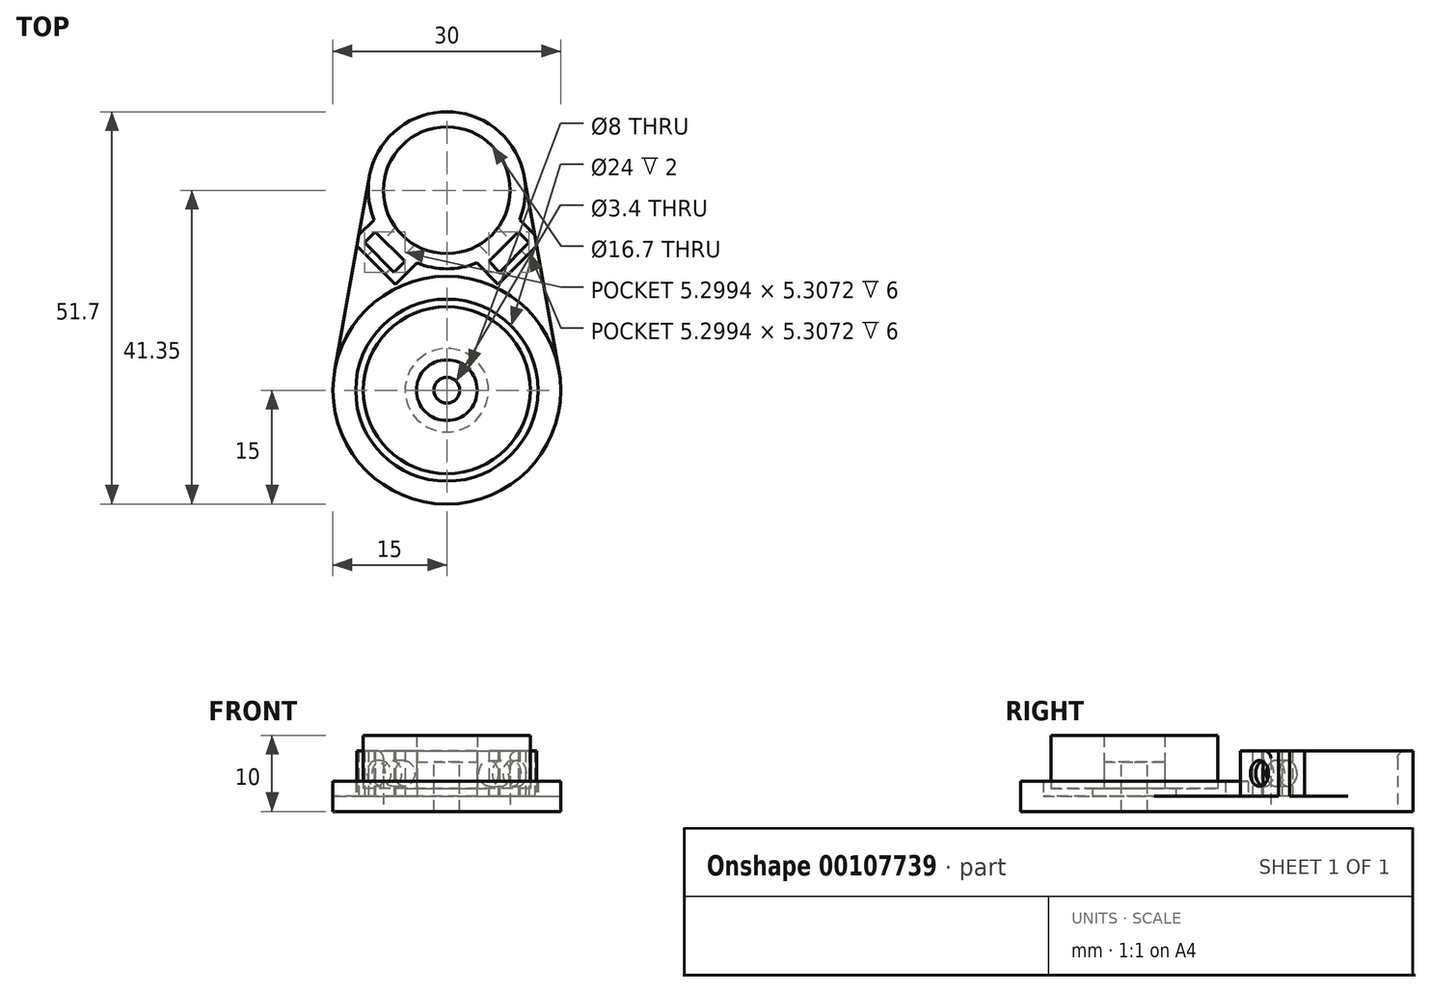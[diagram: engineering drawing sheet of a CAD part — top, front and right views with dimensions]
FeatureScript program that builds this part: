
annotation { "Feature Type Name" : "Feature", "Feature Type Description" : "" }
export const myFeature = defineFeature(function(context is Context, id is Id, definition is map)
    precondition{}
    {
        {
            assignVariable(context, id + "F0", {"name" : "BearingHeight", "anyValue" : 7});
        }
        {
            var Q0;
            Q0=qCreatedBy(makeId("Front.planeOp"),FACE);
            var sketch = newSketch(context, id + "F1", { "sketchPlane" : qUnion([Q0])});
            skLineSegment(sketch, "E0", {"start": v(0, 0) * mm, "end": v(0, 6.5) * mm});
            skLineSegment(sketch, "E1", {"start": v(0, 6.5) * mm, "end": v(4, 6.5) * mm});
            skLineSegment(sketch, "E2", {"start": v(4, 6.5) * mm, "end": v(4, 3) * mm});
            skLineSegment(sketch, "E3", {"start": v(4, 3) * mm, "end": v(5.5, 3) * mm});
            skLineSegment(sketch, "E4", {"start": v(5.5, 3) * mm, "end": v(5.5, 2) * mm});
            skLineSegment(sketch, "E5", {"start": v(5.5, 2) * mm, "end": v(11, 2) * mm});
            skLineSegment(sketch, "E6", {"start": v(11, 2) * mm, "end": v(12, 2) * mm});
            skLineSegment(sketch, "E7", {"start": v(12, 2) * mm, "end": v(12, 4) * mm});
            skLineSegment(sketch, "E8", {"start": v(12, 4) * mm, "end": v(15, 4) * mm});
            skLineSegment(sketch, "E9", {"start": v(15, 4) * mm, "end": v(15, 0) * mm});
            skLineSegment(sketch, "E10", {"start": v(15, 0) * mm, "end": v(0, 0) * mm});
            skSolve(sketch);
        }
        {
            var Q0;
            Q0=qSketchRegion(id+"F1",true);
            var Q1;
            Q1=sQuery(id+"F1.wireOp",EDGE,"E0");
            revolve(context, id + "F2", {"entities" : qUnion([Q0]), "axis" : qUnion([Q1]), "revolveType" : RevolveType.FULL});
        }
        {
            var Q0;
            Q0=makeQuery(id+"F2.opRevolve","SWEPT_FACE",FACE,{"disambiguationData":[OSD([sQuery(id+"F1.wireOp",EDGE,"E1")])]});
            var sketch = newSketch(context, id + "F3", { "sketchPlane" : qUnion([Q0])});
            skCircle(sketch, "E11", {"center": v(0, 0) * mm, "radius": 1.7 * mm});
            skSolve(sketch);
        }
        {
            var Q0;
            Q0=makeQuery(id+"F3.imprint","IMPRINT",FACE,{"disambiguationData":[TD([[makeQuery(id+"F3.imprint","IMPRINT",EDGE,{"derivedFrom":sQuery(id+"F3.wireOp",EDGE,"E11")}),1.0]])]});
            extrude(context, id + "F4", {"entities" : qUnion([Q0]), "operationType" : NewBodyOperationType.REMOVE, "endBound" : BoundingType.UP_TO_NEXT, "oppositeDirection" : true, "depth" : 25 * mm});
        }
        {
            var Q0;
            Q0=makeQuery(id+"F2.opRevolve","SWEPT_FACE",FACE,{"disambiguationData":[OSD([sQuery(id+"F1.wireOp",EDGE,"E10")])]});
            var sketch = newSketch(context, id + "F5", { "sketchPlane" : qUnion([Q0])});
            skCircle(sketch, "E12.0", {"center": v(0, 0) * mm, "radius": 15 * mm});
            skLineSegment(sketch, "E13", {"start": v(0, -26.35) * mm, "end": v(0, 0) * mm, "construction": true});
            skCircle(sketch, "E14", {"center": v(0, -26.35) * mm, "radius": 10.35 * mm});
            skLineSegment(sketch, "E15", {"start": v(-14.76, -2.65) * mm, "end": v(-10.19, -28.18) * mm});
            skLineSegment(sketch, "E16", {"start": v(14.76, -2.65) * mm, "end": v(10.19, -28.18) * mm});
            skCircle(sketch, "E17", {"center": v(0, -26.35) * mm, "radius": 8.35 * mm});
            skLineSegment(sketch, "E18", {"start": v(-3.94, -16.78) * mm, "end": v(-6.77, -13.95) * mm});
            skLineSegment(sketch, "E19", {"start": v(-6.77, -13.95) * mm, "end": v(-12.42, -19.62) * mm});
            skLineSegment(sketch, "E20", {"start": v(-12.42, -19.62) * mm, "end": v(-9.58, -22.44) * mm});
            skLineSegment(sketch, "E21", {"start": v(0, -26.35) * mm, "end": v(-9.6, -16.79) * mm, "construction": true});
            skLineSegment(sketch, "E22.bottom", {"start": v(-9.41, -20.85) * mm, "end": v(-5.53, -16.96) * mm});
            skLineSegment(sketch, "E22.top", {"start": v(-10.83, -19.44) * mm, "end": v(-6.94, -15.55) * mm});
            skLineSegment(sketch, "E22.left", {"start": v(-9.41, -20.85) * mm, "end": v(-10.83, -19.44) * mm});
            skLineSegment(sketch, "E22.right", {"start": v(-5.53, -16.96) * mm, "end": v(-6.94, -15.55) * mm});
            skPoint(sketch, "E22.middle", {"position": v(-8.18, -18.2) * mm});
            skLineSegment(sketch, "E23.MirrorCS", {"start": v(5.53, -16.96) * mm, "end": v(6.94, -15.55) * mm});
            skLineSegment(sketch, "E24.MirrorCS", {"start": v(3.94, -16.78) * mm, "end": v(6.77, -13.95) * mm});
            skPoint(sketch, "E25.MirrorP", {"position": v(8.18, -18.2) * mm});
            skLineSegment(sketch, "E26.MirrorCS", {"start": v(12.42, -19.62) * mm, "end": v(9.58, -22.44) * mm});
            skLineSegment(sketch, "E27.MirrorCS", {"start": v(9.41, -20.85) * mm, "end": v(10.83, -19.44) * mm});
            skLineSegment(sketch, "E28.MirrorCS", {"start": v(10.83, -19.44) * mm, "end": v(6.94, -15.55) * mm});
            skLineSegment(sketch, "E29.MirrorCS", {"start": v(6.77, -13.95) * mm, "end": v(12.42, -19.62) * mm});
            skLineSegment(sketch, "E30.MirrorCS", {"start": v(9.41, -20.85) * mm, "end": v(5.53, -16.96) * mm});
            skSolve(sketch);
        }
        {
            var Q0;
            {var subQ0=sQuery(id+"F5.wireOp",EDGE,"E16");Q0=makeQuery(id+"F5.imprint","IMPRINT",FACE,{"disambiguationData":[TD([[makeQuery(id+"F5.imprint","IMPRINT",EDGE,{"derivedFrom":subQ0}),-1.0]])]});}
            var Q1;
            Q1=makeQuery(id+"F5.imprint","IMPRINT",FACE,{"disambiguationData":[TD([[makeQuery(id+"F5.imprint","IMPRINT",EDGE,{"derivedFrom":sQuery(id+"F5.wireOp",EDGE,"E17")}),-1.0]])]});
            var Q2;
            {var subQ0=sQuery(id+"F5.wireOp",EDGE,"E18");Q2=makeQuery(id+"F5.imprint","IMPRINT",FACE,{"disambiguationData":[TD([[makeQuery(id+"F5.imprint","IMPRINT",EDGE,{"derivedFrom":subQ0}),1.0]])]});}
            var Q3;
            {var subQ1=sQuery(id+"F5.wireOp",EDGE,"E22.bottom");Q3=makeQuery(id+"F5.imprint","IMPRINT",FACE,{"disambiguationData":[TD([[makeQuery(id+"F5.imprint","IMPRINT",EDGE,{"derivedFrom":subQ1}),1.0]])]});}
            var Q4;
            {var subQ0=sQuery(id+"F5.wireOp",EDGE,"E15");var subQ1=sQuery(id+"F5.wireOp",EDGE,"E14");var subQ2=makeQuery(id+"F5.imprint","INTERSECT",VERTEX,{"derivedFrom":[subQ1,subQ0]});Q4=makeQuery(id+"F5.imprint","IMPRINT",FACE,{"disambiguationData":[TD([[makeQuery(id+"F5.imprint","IMPRINT",EDGE,{"disambiguationData":[TD([[subQ2,1.0]])],"derivedFrom":subQ1}),-1.0]])]});}
            var Q5;
            Q5=makeQuery(id+"F5.imprint","IMPRINT",FACE,{"disambiguationData":[TD([[makeQuery(id+"F5.imprint","IMPRINT",EDGE,{"derivedFrom":makeQuery(id+"F4.boolean.opBoolean","COPY",EDGE,{"derivedFrom":makeQuery(id+"F4.opExtrude","TWEAK_EDGE",EDGE,{"derivedFrom":[makeQuery(id+"F2.opRevolve","SWEPT_FACE",FACE,{"disambiguationData":[OSD([sQuery(id+"F1.wireOp",EDGE,"E10")])]}),makeQuery(id+"F3.imprint","IMPRINT",EDGE,{"derivedFrom":sQuery(id+"F3.wireOp",EDGE,"E11")})]})})}),-1.0]])]});
            var Q6;
            Q6=makeQuery(id+"F2.opRevolve","SWEPT_FACE",FACE,{"disambiguationData":[OSD([sQuery(id+"F1.wireOp",EDGE,"E10")])]});
            var Q7;
            Q7=makeQuery(id+"F5.imprint","IMPRINT",FACE,{"disambiguationData":[TD([[makeQuery(id+"F5.imprint","IMPRINT",EDGE,{"derivedFrom":sQuery(id+"F5.wireOp",EDGE,"E23.MirrorCS")}),1.0]])]});
            var Q8;
            Q8=makeQuery(id+"F5.imprint","IMPRINT",FACE,{"disambiguationData":[TD([[makeQuery(id+"F5.imprint","IMPRINT",EDGE,{"derivedFrom":sQuery(id+"F5.wireOp",EDGE,"E23.MirrorCS")}),-1.0]])]});
            var Q9;
            {var subQ10=sQuery(id+"F5.wireOp",EDGE,"E18");Q9=makeQuery(id+"F5.imprint","IMPRINT",FACE,{"disambiguationData":[TD([[makeQuery(id+"F5.imprint","IMPRINT",EDGE,{"derivedFrom":subQ10}),-1.0]])]});}
            var Q10;
            Q10=makeQuery(id+"F2.opRevolve","SWEPT_FACE",FACE,{"disambiguationData":[OSD([sQuery(id+"F1.wireOp",EDGE,"E5"),sQuery(id+"F1.wireOp",EDGE,"E6")])]});
            extrude(context, id + "F6", {"entities" : qUnion([Q0, Q1, Q2, Q3, Q4, Q5, Q6, Q7, Q8, Q9]), "operationType" : NewBodyOperationType.ADD, "endBound" : BoundingType.UP_TO_SURFACE, "oppositeDirection" : true, "endBoundEntityFace" : qUnion([Q10]), "depth" : 25 * mm});
        }
        {
            var Q0;
            Q0=makeQuery(id+"F5.imprint","IMPRINT",FACE,{"disambiguationData":[TD([[makeQuery(id+"F5.imprint","IMPRINT",EDGE,{"derivedFrom":sQuery(id+"F5.wireOp",EDGE,"E17")}),-1.0]])]});
            var Q1;
            {var subQ0=sQuery(id+"F5.wireOp",EDGE,"E18");Q1=makeQuery(id+"F5.imprint","IMPRINT",FACE,{"disambiguationData":[TD([[makeQuery(id+"F5.imprint","IMPRINT",EDGE,{"derivedFrom":subQ0}),1.0]])]});}
            var Q2;
            Q2=makeQuery(id+"F5.imprint","IMPRINT",FACE,{"disambiguationData":[TD([[makeQuery(id+"F5.imprint","IMPRINT",EDGE,{"derivedFrom":sQuery(id+"F5.wireOp",EDGE,"E23.MirrorCS")}),1.0]])]});
            extrude(context, id + "F7", {"entities" : qUnion([Q0, Q1, Q2]), "operationType" : NewBodyOperationType.ADD, "oppositeDirection" : true, "depth" : 8 * mm});
        }
        {
            var Q0;
            Q0=makeQuery(id+"F7.opExtrude","SWEPT_FACE",FACE,{"disambiguationData":[OSD([sQuery(id+"F5.wireOp",EDGE,"E19")])]});
            var sketch = newSketch(context, id + "F8", { "sketchPlane" : qUnion([Q0])});
            skLineSegment(sketch, "E31", {"start": v(-14.66, 5) * mm, "end": v(-21.83, 5) * mm, "construction": true});
            skPoint(sketch, "E32", {"position": v(-18.24, 5) * mm});
            skCircle(sketch, "E33", {"center": v(-18.24, 5) * mm, "radius": 1.7 * mm});
            skSolve(sketch);
        }
        {
            var Q0;
            Q0=makeQuery(id+"F8.imprint","IMPRINT",FACE,{"disambiguationData":[TD([[makeQuery(id+"F8.imprint","IMPRINT",EDGE,{"derivedFrom":sQuery(id+"F8.wireOp",EDGE,"E33")}),1.0]])]});
            var Q1;
            {var subQ0=sQuery(id+"F5.wireOp",EDGE,"E17");Q1=makeQuery(id+"F7.boolean.opBoolean","MERGE",FACE,{"derivedFrom":[makeQuery(id+"F6.opExtrude","SWEPT_FACE",FACE,{"disambiguationData":[OSD([subQ0])]}),makeQuery(id+"F7.opExtrude","SWEPT_FACE",FACE,{"disambiguationData":[OSD([subQ0])]})]});}
            extrude(context, id + "F9", {"entities" : qUnion([Q0]), "operationType" : NewBodyOperationType.REMOVE, "endBound" : BoundingType.UP_TO_SURFACE, "oppositeDirection" : true, "endBoundEntityFace" : qUnion([Q1]), "depth" : 25 * mm});
        }
        {
            var Q0;
            Q0=makeQuery(id+"F7.opExtrude","SWEPT_FACE",FACE,{"disambiguationData":[OSD([sQuery(id+"F5.wireOp",EDGE,"E29.MirrorCS")])]});
            var sketch = newSketch(context, id + "F10", { "sketchPlane" : qUnion([Q0])});
            skLineSegment(sketch, "E34", {"start": v(18.24, 2) * mm, "end": v(18.24, 8) * mm, "construction": true});
            skPoint(sketch, "E35", {"position": v(18.24, 5) * mm});
            skCircle(sketch, "E36", {"center": v(18.24, 5) * mm, "radius": 1.7 * mm});
            skSolve(sketch);
        }
        {
            var Q0;
            Q0=makeQuery(id+"F10.imprint","IMPRINT",FACE,{"disambiguationData":[TD([[makeQuery(id+"F10.imprint","IMPRINT",EDGE,{"derivedFrom":sQuery(id+"F10.wireOp",EDGE,"E36")}),1.0]])]});
            var Q1;
            {var subQ0=sQuery(id+"F5.wireOp",EDGE,"E17");Q1=makeQuery(id+"F7.boolean.opBoolean","MERGE",FACE,{"derivedFrom":[makeQuery(id+"F6.opExtrude","SWEPT_FACE",FACE,{"disambiguationData":[OSD([subQ0])]}),makeQuery(id+"F7.opExtrude","SWEPT_FACE",FACE,{"disambiguationData":[OSD([subQ0])]})]});}
            extrude(context, id + "F11", {"entities" : qUnion([Q0]), "operationType" : NewBodyOperationType.REMOVE, "endBound" : BoundingType.UP_TO_SURFACE, "oppositeDirection" : true, "endBoundEntityFace" : qUnion([Q1]), "depth" : 25 * mm});
        }
        {
            var Q0;
            Q0=makeQuery(id+"F2.opRevolve","SWEPT_FACE",FACE,{"disambiguationData":[OSD([sQuery(id+"F1.wireOp",EDGE,"E3")])]});
            var sketch = newSketch(context, id + "F12", { "sketchPlane" : qUnion([Q0])});
            skCircle(sketch, "E37.0", {"center": v(0, 0) * mm, "radius": 4 * mm});
            skCircle(sketch, "E38", {"center": v(0, 0) * mm, "radius": 11 * mm});
            skSolve(sketch);
        }
        {
            var Q0;
            Q0=qSketchRegion(id+"F12",true);
            extrude(context, id + "F13", {"entities" : qUnion([Q0]), "depth" : (getVariable(context, 'BearingHeight')) * mm});
        }
        {
            var Q0;
            Q0=makeQuery(id+"F7.opExtrude","CAP_EDGE",EDGE,{"disambiguationData":[OSD([sQuery(id+"F5.wireOp",EDGE,"E17")])],"isStart":false});
            fillet(context, id + "F14", {"entities" : qUnion([Q0]), "radius" : 1 * mm, "tangentPropagation" : true, "allowEdgeOverflow" : false});
        }
    });
